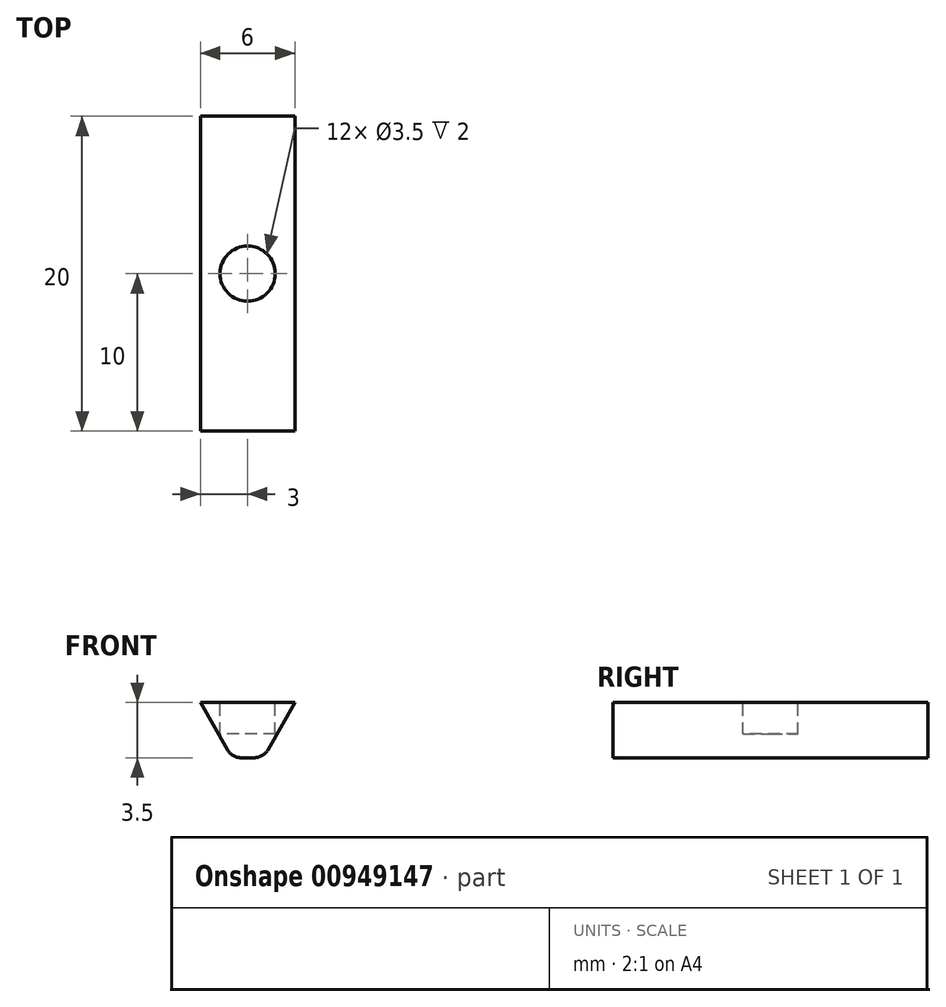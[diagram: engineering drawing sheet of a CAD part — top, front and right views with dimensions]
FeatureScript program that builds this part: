
annotation { "Feature Type Name" : "Feature", "Feature Type Description" : "" }
export const myFeature = defineFeature(function(context is Context, id is Id, definition is map)
    precondition{}
    {
        {
            var Q0;
            Q0=qCreatedBy(makeId("Front.planeOp"),FACE);
            var sketch = newSketch(context, id + "F0", { "sketchPlane" : qUnion([Q0])});
            skLineSegment(sketch, "E0", {"start": v(-1, 0) * mm, "end": v(1, 0) * mm});
            skLineSegment(sketch, "E1", {"start": v(1, 0) * mm, "end": v(3, 3.5) * mm});
            skLineSegment(sketch, "E2", {"start": v(3, 3.5) * mm, "end": v(-3, 3.5) * mm});
            skLineSegment(sketch, "E3", {"start": v(-3, 3.5) * mm, "end": v(-1, 0) * mm});
            skPoint(sketch, "E4", {"position": v(0, 0) * mm});
            skPoint(sketch, "E5", {"position": v(0, 3.5) * mm});
            skSolve(sketch);
        }
        {
            var Q0;
            Q0 = qSketchRegion(id + "F0", true);
            extrude(context, id + "F1", {"entities" : qUnion([Q0]), "endBound" : BoundingType.SYMMETRIC, "depth" : 20 * mm, "offsetDistance" : 25 * mm});
        }
        {
            var Q0;
            Q0=makeQuery(id+"F1.opExtrude","SWEPT_FACE",FACE,{"disambiguationData":[OSD([sQuery(id+"F0.wireOp",EDGE,"E2")])]});
            var sketch = newSketch(context, id + "F2", { "sketchPlane" : qUnion([Q0])});
            skCircle(sketch, "E6", {"center": v(0, 0) * mm, "radius": 1.75 * mm});
            skSolve(sketch);
        }
        {
            var Q0;
            Q0 = qSketchRegion(id + "F2", true);
            extrude(context, id + "F3", {"entities" : qUnion([Q0]), "operationType" : NewBodyOperationType.REMOVE, "oppositeDirection" : true, "depth" : 2 * mm, "offsetDistance" : 25 * mm});
        }
        {
            var Q0;
            Q0=makeQuery(id+"F1.opExtrude","SWEPT_EDGE",EDGE,{"disambiguationData":[OSD([sQuery(id+"F0.wireOp",EDGE,"E0"),sQuery(id+"F0.wireOp",EDGE,"E1")])]});
            var Q1;
            Q1=makeQuery(id+"F1.opExtrude","SWEPT_EDGE",EDGE,{"disambiguationData":[OSD([sQuery(id+"F0.wireOp",EDGE,"E0"),sQuery(id+"F0.wireOp",EDGE,"E3")])]});
            fillet(context, id + "F4", {"entities" : qUnion([Q0, Q1]), "radius" : 1 * mm, "tangentPropagation" : true, "allowEdgeOverflow" : false});
        }
    });
